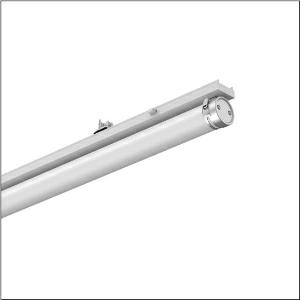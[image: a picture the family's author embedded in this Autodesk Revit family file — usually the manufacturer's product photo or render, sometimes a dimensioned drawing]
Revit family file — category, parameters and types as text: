
# Revit family: monsun_r__31_tube_51ft10mn4a0atr1_8ef5
name_source: partatom
category: Lighting Fixtures
units: mm (PartAtom-declared; Revit-internal decimal feet)

## family parameters
Cut with Voids When Loaded = No
Host = Face
Light Source = No
Part Type = Normal
Room Calculation Point = No
Round Connector Dimension = Use Diameter
Shared = No

## types (1)
- --- (1 x LED, 10000 lm, 58 W, 4000K)
    Apparent Load = 58 VA
    CIE Flux Codes = 42 71 90 91 100
    Color Rendering = 80
    Color Temperature = 4000K
    Default Elevation = 1800 mm
    Description = Monsun® 31 Tube, tubular luminaire, primary optical cover: diffuser, of PMMA, light emission: direct distribution, primary light characteristic: symmetric, LED, rated luminous flux: 10.000lm, luminous efficacy: 172lm/W, light colour: 840, colour temperature: 4000K, with with 1 terminal, 3-pole, max. 2.5mm², mains connection: 220..240V, AC, 50/60Hz, rated input power: 58W, housing, cylindrical, of PMMA, semi-transparent, matt white, with luminaire and ceiling fastening, V4A, mounting with brackets of stainless steel, length: 1.495mm, diameter: 75mm, end cap, of stainless steel (V4A), protection rating (complete): IP20, protection rating (lamp compartment): IP67/69K, insulation class (complete): insulation class I (protective earthing), certification: CE, UKCA, impact resistance: IK07, permissible operating ambient temperature: -20..+40°C, corresponds to IFS (International Featured Standards) requirements for safety and quality in the food industry, contact your sales advisor before using the luminaires in applications with unclear chemical exposure, large temperature fluctuations or condensation-forming humidity, packaging unit: 1 piece
    Height = 118 mm
    Lamp = 1 x LED
    Lamp Light Flux = 10000 lm
    Lamp Power = 58 W
    Lamp count = 1
    Length = 1495 mm
    Luminous efficacy = 172 lm/W
    Manufacturer = Siteco
    ModVariant = No
    Model = 51FT10MN4A0ATR1
    Mounting Place = Ceiling
    Mounting Type = Pendant
    Number of Poles = 1
    OnlyDefault = Yes
    Power Factor = 1
    Product Name = Monsun® 31 Tube
    Product group = tubular luminaire
    ProductGroupID = 906
    Protection Class = Protection class I
    Protection Degree = IP 20
    RLX_Detail_Level = 1
    RLX_Emergency_Light_Flux = 0 lm
    RLX_Emergency_Type = 0
    RLX_Emergency_Type_DB = No
    RlxData = <blob elided: 32305 chars, md5=27e92b2e>
    Socket = socket
    Standby Power = 0 W
    System Light Flux = 10000 lm
    System Power = 58 W
    Type Comments = factory setting: luminous flux: 100 % | (OFF | OFF | OFF | OFF) | 350 mA
    Type Image = l_1007227.jpg
    URL = http://relux.com
    VarID = @adj_092747
    Voltage = 0 V
    Weight = 0.00 kg
    Width = 75 mm

## geometry (parser evidence)
native form markers: Blend x4, Sweep x11
no freeform markers — native parametric forms only
